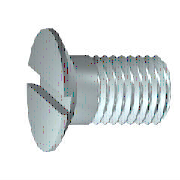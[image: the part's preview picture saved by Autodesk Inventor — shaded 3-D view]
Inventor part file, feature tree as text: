
AUTODESK INVENTOR PART (.ipt)
format: ipt  version: 2017 (Build 210142000, 142)  size: 172,544 bytes
history: native  units: mm (DEFAULTED — no unit token found)
features: sketch x2, extrude x1, plane x1
ambient origin geometry x7: Origin, YZ Plane, XZ Plane, X Axis, Y Axis, Z Axis, Center Point
bodies: Solid1 (feature_tree), Body (feature_tree)
feature tree (4):
  extrude  "Slot"  Depth=4.0mm
  plane  "Work Plane1"
  sketch  "Sketch1"  dims[d0=6.0mm d1=45.0deg d2=0.24538mm d3=4.0mm d4=1.2mm d5=1.50924mm]
  sketch  "Sketch2"  dims[d6=2.0mm d7=3.5mm d19=90.0deg d8=0.4mm d9=0.0mm d10=4.0mm d11=0.0mm d12=0.24538mm d13=0.12269mm d15=0.7mm d16=3.5mm d17=0.0mm d35=45.0deg d39=0.0mm d40=0.0mm]
